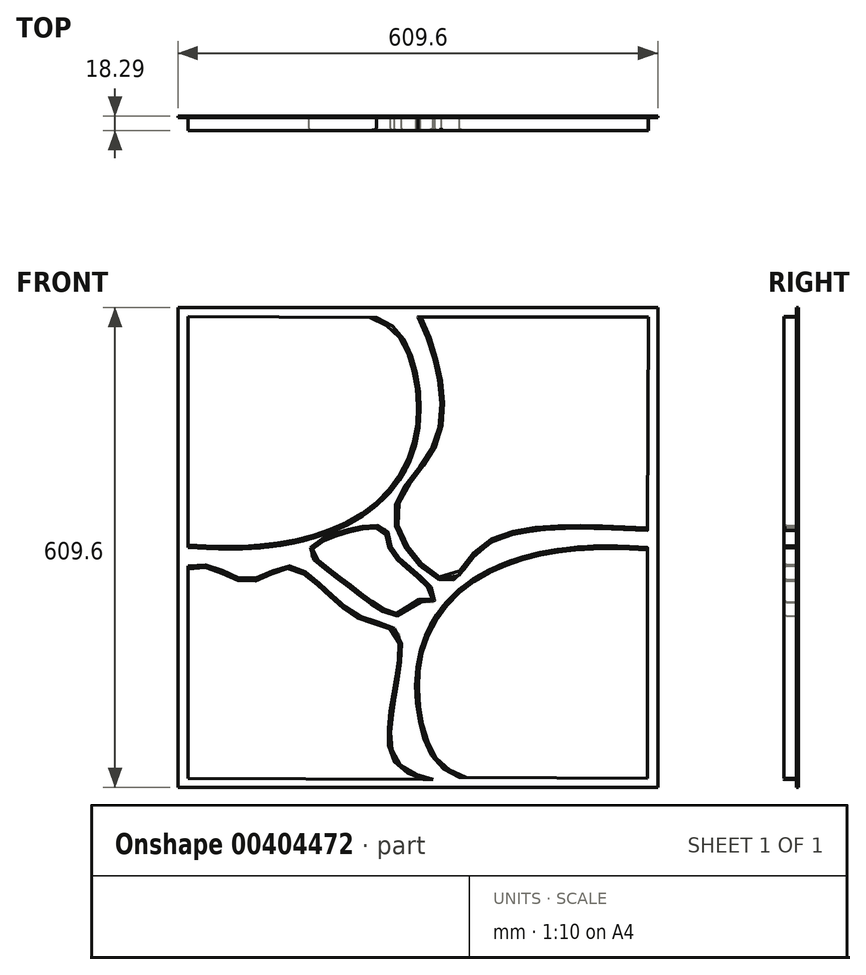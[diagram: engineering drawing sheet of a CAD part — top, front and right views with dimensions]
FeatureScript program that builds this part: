
annotation { "Feature Type Name" : "Feature", "Feature Type Description" : "" }
export const myFeature = defineFeature(function(context is Context, id is Id, definition is map)
    precondition{}
    {
        {
            var Q0;
            Q0=qCreatedBy(makeId("Front.planeOp"),FACE);
            var sketch = newSketch(context, id + "F0", { "sketchPlane" : qUnion([Q0])});
            skLineSegment(sketch, "E0.bottom", {"start": v(476.25, -476.25) * mm, "end": v(-476.25, -476.25) * mm});
            skLineSegment(sketch, "E0.top", {"start": v(476.25, 476.25) * mm, "end": v(-476.25, 476.25) * mm});
            skLineSegment(sketch, "E0.left", {"start": v(476.25, -476.25) * mm, "end": v(476.25, 476.25) * mm});
            skLineSegment(sketch, "E0.right", {"start": v(-476.25, -476.25) * mm, "end": v(-476.25, 476.25) * mm});
            skPoint(sketch, "E0.middle", {"position": v(0, 0) * mm});
            skSolve(sketch);
        }
        {
            var Q0;
            Q0=makeQuery(id+"F0.imprint","IMPRINT",FACE,{"disambiguationData":[TD([[makeQuery(id+"F0.imprint","IMPRINT",EDGE,{"derivedFrom":sQuery(id+"F0.wireOp",EDGE,"E0.bottom")}),-1.0]])]});
            extrude(context, id + "F1", {"entities" : qUnion([Q0]), "depth" : 3.17 * mm});
        }
        {
            var Q0;
            Q0=makeQuery(id+"F1.opExtrude","CAP_FACE",FACE,{"disambiguationData":[OSD([sQuery(id+"F0.wireOp",EDGE,"E0.bottom"),sQuery(id+"F0.wireOp",EDGE,"E0.top"),sQuery(id+"F0.wireOp",EDGE,"E0.left"),sQuery(id+"F0.wireOp",EDGE,"E0.right")])],"isStart":false});
            var sketch = newSketch(context, id + "F2", { "sketchPlane" : qUnion([Q0])});
            skLineSegment(sketch, "E1.bottom", {"start": v(457.2, -457.2) * mm, "end": v(-457.2, -457.2) * mm});
            skLineSegment(sketch, "E1.top", {"start": v(457.2, 457.2) * mm, "end": v(-457.2, 457.2) * mm});
            skLineSegment(sketch, "E1.left", {"start": v(457.2, -457.2) * mm, "end": v(457.2, 457.2) * mm});
            skLineSegment(sketch, "E1.right", {"start": v(-457.2, -457.2) * mm, "end": v(-457.2, 457.2) * mm});
            skPoint(sketch, "E1.middle", {"position": v(0, 0) * mm});
            skSolve(sketch);
        }
        {
            var Q0;
            Q0=makeQuery(id+"F2.imprint","IMPRINT",FACE,{"disambiguationData":[TD([[makeQuery(id+"F2.imprint","IMPRINT",EDGE,{"derivedFrom":sQuery(id+"F2.wireOp",EDGE,"E1.bottom")}),-1.0]])]});
            var sketch = newSketch(context, id + "F3", { "sketchPlane" : qUnion([Q0])});
            skLineSegment(sketch, "E2", {"start": v(-455.79, 458.3) * mm, "end": v(-455.79, 0) * mm});
            skFitSpline(sketch, "E3", {"points": [v(-455.79, 0) * mm, v(-308.05, 0) * mm, v(-111.64, 61.2) * mm, v(0, 224.31) * mm, v(-29.66, 416.46) * mm, v(-82.6, 456.6) * mm], "startDerivative": vector(723.43, -41.06) * mm, "endDerivative": vector(-433.72, 194.94) * mm});
            skLineSegment(sketch, "E4", {"start": v(-455.79, 458.3) * mm, "end": v(-82.6, 456.6) * mm});
            skLineSegment(sketch, "E5", {"start": v(0, 110.8) * mm, "end": v(0, -108.53) * mm, "construction": true});
            skLineSegment(sketch, "E6", {"start": v(-88.8, 0) * mm, "end": v(94.97, 0) * mm, "construction": true});
            skLineSegment(sketch, "E7.MirrorCS", {"start": v(455.79, -458.3) * mm, "end": v(455.79, 0) * mm});
            skFitSpline(sketch, "E8.MirrorCS", {"points": [v(455.79, 0) * mm, v(308.05, 0) * mm, v(111.64, -61.2) * mm, v(0, -224.31) * mm, v(29.66, -416.46) * mm, v(82.6, -456.6) * mm], "startDerivative": vector(-723.43, 41.06) * mm, "endDerivative": vector(433.72, -194.94) * mm});
            skLineSegment(sketch, "E9.MirrorCS", {"start": v(455.79, -458.3) * mm, "end": v(82.6, -456.6) * mm});
            skPoint(sketch, "E10.MirrorCS.start.orphan", {"position": v(-455.79, -458.3) * mm});
            skPoint(sketch, "E11.MirrorCS.end.orphan", {"position": v(-82.6, -456.6) * mm});
            skLineSegment(sketch, "E12", {"start": v(-455.79, -458.3) * mm, "end": v(-455.79, -36.97) * mm});
            skFitSpline(sketch, "E13", {"points": [v(-455.79, -36.97) * mm, v(-409, -36.97) * mm, v(-331.98, -63.16) * mm, v(-250.33, -36.97) * mm, v(-117.85, -134.8) * mm, v(-36.2, -174.08) * mm, v(-51.6, -401.3) * mm, v(29.66, -460.6) * mm], "startDerivative": vector(467.73, 87.1) * mm, "endDerivative": vector(781.2, -217.56) * mm});
            skLineSegment(sketch, "E14", {"start": v(-455.79, -458.3) * mm, "end": v(29.66, -460.6) * mm});
            skFitSpline(sketch, "E15", {"points": [v(0, 457.53) * mm, v(26.19, 393.6) * mm, v(33.9, 210.28) * mm, v(-46.98, 60.08) * mm, v(57, -67.01) * mm, v(129.4, 0) * mm, v(455.99, 33.9) * mm], "startDerivative": vector(232.75, -478.06) * mm, "endDerivative": vector(1670.48, -82.36) * mm});
            skLineSegment(sketch, "E16", {"start": v(0, 457.53) * mm, "end": v(457.53, 457.53) * mm});
            skLineSegment(sketch, "E17", {"start": v(457.53, 457.53) * mm, "end": v(455.99, 33.9) * mm});
            skFitSpline(sketch, "E18", {"points": [v(-213.36, 0) * mm, v(-195.64, -33.9) * mm, v(-117.85, -93.2) * mm, v(-36.2, -134.8) * mm, v(0, -108.53) * mm, v(30.04, -108.53) * mm, v(26.14, -79.35) * mm, v(-52.38, 0) * mm, v(-69.18, 41.53) * mm, v(-213.36, 0) * mm]});
            skSolve(sketch);
        }
        {
            var Q0;
            Q0 = qSketchRegion(id + "F3", true);
            extrude(context, id + "F4", {"entities" : qUnion([Q0]), "operationType" : NewBodyOperationType.ADD, "depth" : 25.4 * mm});
        }
        {
            var Q0;
            Q0=makeQuery(id+"F4.opExtrude","CAP_EDGE",EDGE,{"disambiguationData":[OSD([sQuery(id+"F3.wireOp",EDGE,"E3")])],"isStart":false});
            var Q1;
            Q1=makeQuery(id+"F4.opExtrude","CAP_FACE",FACE,{"disambiguationData":[OSD([sQuery(id+"F3.wireOp",EDGE,"E18")])],"isStart":false});
            var Q2;
            Q2=makeQuery(id+"F4.opExtrude","CAP_EDGE",EDGE,{"disambiguationData":[OSD([sQuery(id+"F3.wireOp",EDGE,"E13")])],"isStart":false});
            var Q3;
            Q3=makeQuery(id+"F4.opExtrude","CAP_EDGE",EDGE,{"disambiguationData":[OSD([sQuery(id+"F3.wireOp",EDGE,"E8.MirrorCS")])],"isStart":false});
            var Q4;
            Q4=makeQuery(id+"F4.opExtrude","CAP_EDGE",EDGE,{"disambiguationData":[OSD([sQuery(id+"F3.wireOp",EDGE,"E15")])],"isStart":false});
            fillet(context, id + "F5", {"entities" : qUnion([Q0, Q1, Q2, Q3, Q4]), "radius" : 5.08 * mm, "tangentPropagation" : true, "allowEdgeOverflow" : false});
        }
        {
            var Q0;
            Q0=makeQuery(id+"F1.opExtrude","SWEPT_BODY",BODY,{"disambiguationData":[OSD([sQuery(id+"F0.wireOp",EDGE,"E0.bottom"),sQuery(id+"F0.wireOp",EDGE,"E0.top"),sQuery(id+"F0.wireOp",EDGE,"E0.left"),sQuery(id+"F0.wireOp",EDGE,"E0.right")])]});
            var Q1;
            Q1=sQuery(id+"F2.wireOp",VERTEX,"E1.middle");
            transform(context, id + "F6", {"entities" : qUnion([Q0]), "transformType" : TransformType.SCALE_UNIFORMLY, "scale" : .64, "scalePoint" : qUnion([Q1]), "makeCopy" : false});
        }
    });
